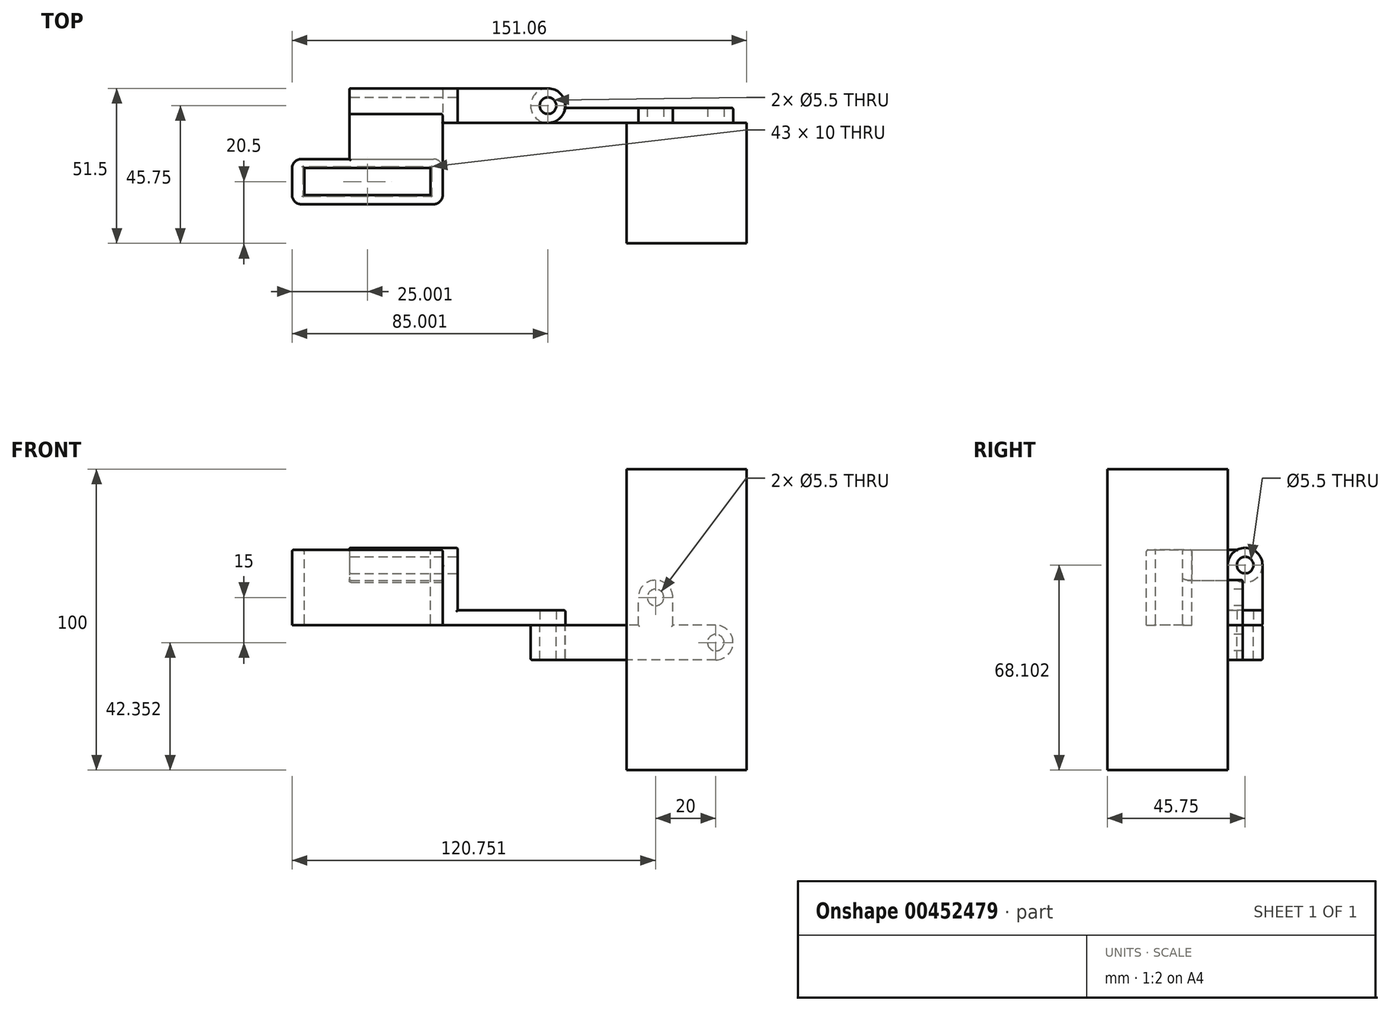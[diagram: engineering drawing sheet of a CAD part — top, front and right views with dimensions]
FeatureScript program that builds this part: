
annotation { "Feature Type Name" : "Feature", "Feature Type Description" : "" }
export const myFeature = defineFeature(function(context is Context, id is Id, definition is map)
    precondition{}
    {
        {
            var Q0;
            Q0=qCreatedBy(makeId("Top.planeOp"),FACE);
            var sketch = newSketch(context, id + "F0", { "sketchPlane" : qUnion([Q0])});
            skLineSegment(sketch, "E0.bottom", {"start": v(-20, 20) * mm, "end": v(20, 20) * mm});
            skLineSegment(sketch, "E0.top", {"start": v(-20, -20) * mm, "end": v(20, -20) * mm});
            skLineSegment(sketch, "E0.left", {"start": v(-20, 20) * mm, "end": v(-20, -20) * mm});
            skLineSegment(sketch, "E0.right", {"start": v(20, 20) * mm, "end": v(20, -20) * mm});
            skPoint(sketch, "E0.middle", {"position": v(0, 0) * mm});
            skSolve(sketch);
        }
        {
            var Q0;
            Q0=makeQuery(id+"F0.imprint","IMPRINT",FACE,{"disambiguationData":[TD([[makeQuery(id+"F0.imprint","IMPRINT",EDGE,{"derivedFrom":sQuery(id+"F0.wireOp",EDGE,"E0.bottom")}),-1.0]])]});
            extrude(context, id + "F1", {"entities" : qUnion([Q0]), "depth" : 100 * mm});
        }
        {
            var Q0;
            Q0=makeQuery(id+"F1.opExtrude","SWEPT_FACE",FACE,{"disambiguationData":[OSD([sQuery(id+"F0.wireOp",EDGE,"E0.bottom")])]});
            var sketch = newSketch(context, id + "F2", { "sketchPlane" : qUnion([Q0])});
            skPoint(sketch, "E1", {"position": v(-9.7, 42.35) * mm});
            skPoint(sketch, "E2", {"position": v(10.3, 57.35) * mm});
            skCircle(sketch, "E3", {"center": v(-9.7, 42.35) * mm, "radius": 5.75 * mm});
            skCircle(sketch, "E4", {"center": v(10.3, 57.35) * mm, "radius": 5.75 * mm});
            skLineSegment(sketch, "E5", {"start": v(-9.7, 48.1) * mm, "end": v(4.56, 48.1) * mm});
            skLineSegment(sketch, "E6", {"start": v(4.56, 48.1) * mm, "end": v(4.56, 57.35) * mm});
            skLineSegment(sketch, "E7", {"start": v(-9.7, 36.6) * mm, "end": v(16.06, 36.6) * mm});
            skLineSegment(sketch, "E8", {"start": v(16.06, 36.6) * mm, "end": v(16.06, 57.35) * mm});
            skLineSegment(sketch, "E9", {"start": v(16.06, 48.1) * mm, "end": v(46.06, 48.1) * mm});
            skLineSegment(sketch, "E10", {"start": v(46.06, 48.1) * mm, "end": v(46.06, 36.6) * mm});
            skLineSegment(sketch, "E11", {"start": v(46.06, 36.6) * mm, "end": v(16.06, 36.6) * mm});
            skSolve(sketch);
        }
        {
            var Q0;
            {var subQ0=sQuery(id+"F2.wireOp",EDGE,"E3");var subQ1=makeQuery(id+"F2.imprint","INTERSECT",VERTEX,{"derivedFrom":[subQ0,sQuery(id+"F2.wireOp",EDGE,"E5")]});Q0=makeQuery(id+"F2.imprint","IMPRINT",FACE,{"disambiguationData":[TD([[makeQuery(id+"F2.imprint","IMPRINT",EDGE,{"disambiguationData":[TD([[subQ1,-1.0]])],"derivedFrom":subQ0}),1.0]])]});}
            var Q1;
            {var subQ0=sQuery(id+"F2.wireOp",EDGE,"E4");var subQ1=makeQuery(id+"F2.imprint","INTERSECT",VERTEX,{"derivedFrom":[subQ0,sQuery(id+"F2.wireOp",EDGE,"E6")]});Q1=makeQuery(id+"F2.imprint","IMPRINT",FACE,{"disambiguationData":[TD([[makeQuery(id+"F2.imprint","IMPRINT",EDGE,{"disambiguationData":[TD([[subQ1,1.0]])],"derivedFrom":subQ0}),1.0]])]});}
            var Q2;
            {var subQ1=sQuery(id+"F2.wireOp",EDGE,"E5");Q2=makeQuery(id+"F2.imprint","IMPRINT",FACE,{"disambiguationData":[TD([[makeQuery(id+"F2.imprint","IMPRINT",EDGE,{"derivedFrom":subQ1}),-1.0]])]});}
            var Q3;
            {var subQ0=sQuery(id+"F2.wireOp",EDGE,"E10");Q3=makeQuery(id+"F2.imprint","IMPRINT",FACE,{"disambiguationData":[TD([[makeQuery(id+"F2.imprint","IMPRINT",EDGE,{"derivedFrom":subQ0}),-1.0]])]});}
            var Q4;
            {var subQ1=sQuery(id+"F2.wireOp",EDGE,"E8");var subQ3=sQuery(id+"F2.wireOp",EDGE,"E9");var subQ4=makeQuery(id+"F2.imprint","INTERSECT",VERTEX,{"derivedFrom":[subQ1,subQ3]});Q4=makeQuery(id+"F2.imprint","IMPRINT",FACE,{"disambiguationData":[TD([[makeQuery(id+"F2.imprint","IMPRINT",EDGE,{"disambiguationData":[TD([[subQ4,1.0]])],"derivedFrom":subQ1}),-1.0]])]});}
            extrude(context, id + "F3", {"entities" : qUnion([Q0, Q1, Q2, Q3, Q4]), "depth" : 5 * mm});
        }
        {
            var Q0;
            Q0=sQuery(id+"F2.wireOp",VERTEX,"E2");
            var Q1;
            Q1=sQuery(id+"F2.wireOp",VERTEX,"E1");
            var Q2;
            Q2=makeQuery(id+"F3.opExtrude","SWEPT_BODY",BODY,{"disambiguationData":[OSD([sQuery(id+"F2.wireOp",EDGE,"E3"),sQuery(id+"F2.wireOp",EDGE,"E4"),sQuery(id+"F2.wireOp",EDGE,"E5"),sQuery(id+"F2.wireOp",EDGE,"E6"),sQuery(id+"F2.wireOp",EDGE,"E7"),sQuery(id+"F2.wireOp",EDGE,"E8"),sQuery(id+"F2.wireOp",EDGE,"E9"),sQuery(id+"F2.wireOp",EDGE,"E10"),sQuery(id+"F2.wireOp",EDGE,"E11")])]});
            hole(context, id + "F4", {"style" : HoleStyle.SIMPLE, "endStyle" : HoleEndStyle.THROUGH, "oppositeDirection" : true, "standardTappedOrClearance" : lookupTablePath({ "standard" : "ISO", "fit" : "Normal", "size" : "M5", "type" : "Clearance" }), "standardBlindInLast" : lookupTablePath({ "fit" : "Standard", "standard" : "ISO", "size" : "M5", "type" : "Clearance" }), "holeDiameter" : 5.5 * mm, "isTappedThrough" : true, "tappedDepth" : 13.2 * mm, "tapClearance" : 3, "startFromSketch" : true, "locations" : qUnion([Q0, Q1]), "scope" : qUnion([Q2])});
        }
        {
            var Q0;
            Q0=makeQuery(id+"F3.opExtrude","SWEPT_FACE",FACE,{"disambiguationData":[OSD([sQuery(id+"F2.wireOp",EDGE,"E9")])]});
            var sketch = newSketch(context, id + "F5", { "sketchPlane" : qUnion([Q0])});
            skPoint(sketch, "E12", {"position": v(-46.06, 25.75) * mm});
            skCircle(sketch, "E13", {"center": v(-46.06, 25.75) * mm, "radius": 5.75 * mm});
            skSolve(sketch);
        }
        {
            var Q0;
            {var subQ1=sQuery(id+"F2.wireOp",EDGE,"E9");var subQ2=makeQuery(id+"F3.opExtrude","SWEPT_EDGE",EDGE,{"disambiguationData":[OSD([subQ1,sQuery(id+"F2.wireOp",EDGE,"E10")])]});Q0=makeQuery(id+"F5.imprint","IMPRINT",FACE,{"disambiguationData":[TD([[makeQuery(id+"F5.imprint","IMPRINT",EDGE,{"derivedFrom":subQ2}),-1.0]])]});}
            var Q1;
            Q1=makeQuery(id+"F3.opExtrude","SWEPT_FACE",FACE,{"disambiguationData":[OSD([sQuery(id+"F2.wireOp",EDGE,"E7"),sQuery(id+"F2.wireOp",EDGE,"E11")])]});
            extrude(context, id + "F6", {"entities" : qUnion([Q0]), "operationType" : NewBodyOperationType.ADD, "endBound" : BoundingType.UP_TO_SURFACE, "oppositeDirection" : true, "endBoundEntityFace" : qUnion([Q1]), "depth" : 25 * mm});
        }
        {
            var Q0;
            Q0=sQuery(id+"F5.wireOp",VERTEX,"E12");
            var Q1;
            Q1=makeQuery(id+"F3.opExtrude","SWEPT_BODY",BODY,{"disambiguationData":[OSD([sQuery(id+"F2.wireOp",EDGE,"E3"),sQuery(id+"F2.wireOp",EDGE,"E4"),sQuery(id+"F2.wireOp",EDGE,"E5"),sQuery(id+"F2.wireOp",EDGE,"E6"),sQuery(id+"F2.wireOp",EDGE,"E7"),sQuery(id+"F2.wireOp",EDGE,"E8"),sQuery(id+"F2.wireOp",EDGE,"E9"),sQuery(id+"F2.wireOp",EDGE,"E10"),sQuery(id+"F2.wireOp",EDGE,"E11")])]});
            hole(context, id + "F7", {"style" : HoleStyle.SIMPLE, "endStyle" : HoleEndStyle.THROUGH, "standardTappedOrClearance" : lookupTablePath({ "standard" : "ISO", "fit" : "Normal", "size" : "M5", "type" : "Clearance" }), "standardBlindInLast" : lookupTablePath({ "fit" : "Standard", "standard" : "ISO", "size" : "M5", "type" : "Clearance" }), "holeDiameter" : 5.5 * mm, "isTappedThrough" : true, "tappedDepth" : 13.2 * mm, "tapClearance" : 3, "startFromSketch" : true, "locations" : qUnion([Q0]), "scope" : qUnion([Q1])});
        }
        {
            var Q0;
            {var subQ1=sQuery(id+"F2.wireOp",EDGE,"E9");var subQ2=makeQuery(id+"F3.opExtrude","CAP_EDGE",EDGE,{"disambiguationData":[OSD([subQ1])],"isStart":true});Q0=makeQuery(id+"F5.imprint","IMPRINT",FACE,{"disambiguationData":[TD([[makeQuery(id+"F5.imprint","IMPRINT",EDGE,{"derivedFrom":subQ2}),-1.0]])]});}
            var sketch = newSketch(context, id + "F8", { "sketchPlane" : qUnion([Q0])});
            skPoint(sketch, "E14", {"position": v(-46.06, 25.75) * mm});
            skCircle(sketch, "E15", {"center": v(-46.06, 25.75) * mm, "radius": 5.75 * mm});
            skLineSegment(sketch, "E16", {"start": v(-46.06, 31.5) * mm, "end": v(-76.06, 31.5) * mm});
            skLineSegment(sketch, "E17", {"start": v(-76.06, 31.5) * mm, "end": v(-76.06, 20) * mm});
            skLineSegment(sketch, "E18", {"start": v(-76.06, 20) * mm, "end": v(-46.06, 20) * mm});
            skSolve(sketch);
        }
        {
            var Q0;
            {var subQ2=sQuery(id+"F8.wireOp",EDGE,"E16");Q0=makeQuery(id+"F8.imprint","IMPRINT",FACE,{"disambiguationData":[TD([[makeQuery(id+"F8.imprint","IMPRINT",EDGE,{"derivedFrom":subQ2}),1.0]])]});}
            var Q1;
            {var subQ0=sQuery(id+"F8.wireOp",EDGE,"E15");var subQ3=makeQuery(id+"F8.imprint","INTERSECT",VERTEX,{"derivedFrom":[subQ0,sQuery(id+"F8.wireOp",EDGE,"E16")]});Q1=makeQuery(id+"F8.imprint","IMPRINT",FACE,{"disambiguationData":[TD([[makeQuery(id+"F8.imprint","IMPRINT",EDGE,{"disambiguationData":[TD([[subQ3,-1.0]])],"derivedFrom":subQ0}),1.0]])]});}
            extrude(context, id + "F9", {"entities" : qUnion([Q0, Q1]), "depth" : 5 * mm});
        }
        {
            var Q0;
            Q0=sQuery(id+"F5.wireOp",VERTEX,"E12");
            var Q1;
            Q1=makeQuery(id+"F9.opExtrude","SWEPT_BODY",BODY,{"disambiguationData":[OSD([sQuery(id+"F8.wireOp",EDGE,"E15"),sQuery(id+"F8.wireOp",EDGE,"E16"),sQuery(id+"F8.wireOp",EDGE,"E17"),sQuery(id+"F8.wireOp",EDGE,"E18")])]});
            hole(context, id + "F10", {"style" : HoleStyle.SIMPLE, "endStyle" : HoleEndStyle.THROUGH, "oppositeDirection" : true, "standardTappedOrClearance" : lookupTablePath({ "standard" : "ISO", "fit" : "Normal", "size" : "M5", "type" : "Clearance" }), "standardBlindInLast" : lookupTablePath({ "fit" : "Standard", "standard" : "ISO", "size" : "M5", "type" : "Clearance" }), "holeDiameter" : 5.5 * mm, "isTappedThrough" : true, "tappedDepth" : 13.2 * mm, "tapClearance" : 3, "startFromSketch" : true, "locations" : qUnion([Q0]), "scope" : qUnion([Q1])});
        }
        {
            var Q0;
            Q0=makeQuery(id+"F9.opExtrude","SWEPT_FACE",FACE,{"disambiguationData":[OSD([sQuery(id+"F8.wireOp",EDGE,"E17")])]});
            var sketch = newSketch(context, id + "F11", { "sketchPlane" : qUnion([Q0])});
            skLineSegment(sketch, "E19.bottom", {"start": v(-31.5, 48.1) * mm, "end": v(-20, 48.1) * mm});
            skLineSegment(sketch, "E19.top", {"start": v(-31.5, 68.1) * mm, "end": v(-20, 68.1) * mm});
            skLineSegment(sketch, "E19.left", {"start": v(-31.5, 48.1) * mm, "end": v(-31.5, 68.1) * mm});
            skLineSegment(sketch, "E19.right", {"start": v(-20, 48.1) * mm, "end": v(-20, 68.1) * mm});
            skCircle(sketch, "E20", {"center": v(-25.75, 68.1) * mm, "radius": 5.75 * mm});
            skSolve(sketch);
        }
        {
            var Q0;
            {var subQ0=sQuery(id+"F11.wireOp",EDGE,"E19.top");Q0=makeQuery(id+"F11.imprint","IMPRINT",FACE,{"disambiguationData":[TD([[makeQuery(id+"F11.imprint","IMPRINT",EDGE,{"derivedFrom":subQ0}),-1.0]])]});}
            var Q1;
            {var subQ0=sQuery(id+"F11.wireOp",EDGE,"E19.top");Q1=makeQuery(id+"F11.imprint","IMPRINT",FACE,{"disambiguationData":[TD([[makeQuery(id+"F11.imprint","IMPRINT",EDGE,{"derivedFrom":subQ0}),1.0]])]});}
            var Q2;
            {var subQ1=makeQuery(id+"F9.opExtrude","CAP_EDGE",EDGE,{"disambiguationData":[OSD([sQuery(id+"F8.wireOp",EDGE,"E17")])],"isStart":false});Q2=makeQuery(id+"F11.imprint","IMPRINT",FACE,{"disambiguationData":[TD([[makeQuery(id+"F11.imprint","IMPRINT",EDGE,{"derivedFrom":subQ1}),1.0]])]});}
            var Q3;
            {var subQ0=sQuery(id+"F11.wireOp",EDGE,"E19.bottom");Q3=makeQuery(id+"F11.imprint","IMPRINT",FACE,{"disambiguationData":[TD([[makeQuery(id+"F11.imprint","IMPRINT",EDGE,{"derivedFrom":subQ0}),1.0]])]});}
            extrude(context, id + "F12", {"entities" : qUnion([Q0, Q1, Q2, Q3]), "operationType" : NewBodyOperationType.ADD, "depth" : 5 * mm});
        }
        {
            var Q0;
            Q0=sQuery(id+"F11.wireOp",VERTEX,"E20.center");
            var Q1;
            Q1=makeQuery(id+"F9.opExtrude","SWEPT_BODY",BODY,{"disambiguationData":[OSD([sQuery(id+"F8.wireOp",EDGE,"E15"),sQuery(id+"F8.wireOp",EDGE,"E16"),sQuery(id+"F8.wireOp",EDGE,"E17"),sQuery(id+"F8.wireOp",EDGE,"E18")])]});
            hole(context, id + "F13", {"style" : HoleStyle.SIMPLE, "endStyle" : HoleEndStyle.THROUGH, "oppositeDirection" : true, "standardTappedOrClearance" : lookupTablePath({ "standard" : "ISO", "fit" : "Normal", "size" : "M5", "type" : "Clearance" }), "standardBlindInLast" : lookupTablePath({ "fit" : "Standard", "standard" : "ISO", "size" : "M5", "type" : "Clearance" }), "holeDiameter" : 5.5 * mm, "isTappedThrough" : true, "tappedDepth" : 13.2 * mm, "tapClearance" : 3, "startFromSketch" : true, "locations" : qUnion([Q0]), "scope" : qUnion([Q1])});
        }
        {
            var Q0;
            Q0=makeQuery(id+"F12.opExtrude","CAP_FACE",FACE,{"disambiguationData":[OSD([sQuery(id+"F11.wireOp",EDGE,"E19.bottom"),sQuery(id+"F11.wireOp",EDGE,"E19.left"),sQuery(id+"F11.wireOp",EDGE,"E19.right"),sQuery(id+"F11.wireOp",EDGE,"E20")])],"isStart":false});
            var sketch = newSketch(context, id + "F14", { "sketchPlane" : qUnion([Q0])});
            skCircle(sketch, "E21", {"center": v(-25.75, 68.1) * mm, "radius": 5.75 * mm});
            skSolve(sketch);
        }
        {
            var Q0;
            {var subQ0=sQuery(id+"F14.wireOp",EDGE,"E21");var subQ1=sQuery(id+"F11.wireOp",EDGE,"E19.left");var subQ2=makeQuery(id+"F14.imprint","INTERSECT",VERTEX,{"derivedFrom":[makeQuery(id+"F12.opExtrude","CAP_EDGE",EDGE,{"disambiguationData":[OSD([subQ1])],"isStart":false}),subQ0]});Q0=makeQuery(id+"F14.imprint","IMPRINT",FACE,{"disambiguationData":[TD([[makeQuery(id+"F14.imprint","IMPRINT",EDGE,{"disambiguationData":[TD([[subQ2,1.0]])],"derivedFrom":subQ0}),1.0]])]});}
            extrude(context, id + "F15", {"entities" : qUnion([Q0]), "depth" : 31 * mm});
        }
        {
            var Q0;
            Q0=makeQuery(id+"F15.opExtrude","CAP_FACE",FACE,{"disambiguationData":[OSD([sQuery(id+"F11.wireOp",EDGE,"E19.bottom"),sQuery(id+"F11.wireOp",EDGE,"E19.left"),sQuery(id+"F11.wireOp",EDGE,"E19.right"),sQuery(id+"F11.wireOp",EDGE,"E20"),sQuery(id+"F13.hole-0.sketch.wireOp",EDGE,"core_line_2"),sQuery(id+"F14.wireOp",EDGE,"E21")])],"isStart":true});
            var sketch = newSketch(context, id + "F16", { "sketchPlane" : qUnion([Q0])});
            skLineSegment(sketch, "E22.bottom", {"start": v(8, 73.15) * mm, "end": v(23, 73.15) * mm});
            skLineSegment(sketch, "E22.top", {"start": v(8, 63.05) * mm, "end": v(23, 63.05) * mm});
            skLineSegment(sketch, "E22.left", {"start": v(8, 73.15) * mm, "end": v(8, 63.05) * mm});
            skLineSegment(sketch, "E22.right", {"start": v(23, 73.15) * mm, "end": v(23, 63.05) * mm});
            skSolve(sketch);
        }
        {
            var Q0;
            {var subQ0=sQuery(id+"F16.wireOp",EDGE,"E22.bottom");Q0=makeQuery(id+"F16.imprint","IMPRINT",FACE,{"disambiguationData":[TD([[makeQuery(id+"F16.imprint","IMPRINT",EDGE,{"derivedFrom":subQ0}),-1.0]])]});}
            extrude(context, id + "F17", {"entities" : qUnion([Q0]), "operationType" : NewBodyOperationType.ADD, "oppositeDirection" : true, "depth" : 31 * mm});
        }
        {
            var Q0;
            Q0=makeQuery(id+"F17.opExtrude","SWEPT_FACE",FACE,{"disambiguationData":[OSD([sQuery(id+"F16.wireOp",EDGE,"E22.bottom")])]});
            var sketch = newSketch(context, id + "F18", { "sketchPlane" : qUnion([Q0])});
            skLineSegment(sketch, "E23.bottom", {"start": v(-81.06, 8) * mm, "end": v(-131.06, 8) * mm});
            skLineSegment(sketch, "E23.top", {"start": v(-81.06, -7) * mm, "end": v(-131.06, -7) * mm});
            skLineSegment(sketch, "E23.left", {"start": v(-81.06, 8) * mm, "end": v(-81.06, -7) * mm});
            skLineSegment(sketch, "E23.right", {"start": v(-131.06, 8) * mm, "end": v(-131.06, -7) * mm});
            skLineSegment(sketch, "E24.bottom", {"start": v(-127.06, 5) * mm, "end": v(-85.06, 5) * mm});
            skLineSegment(sketch, "E24.top", {"start": v(-127.06, -4) * mm, "end": v(-85.06, -4) * mm});
            skLineSegment(sketch, "E24.left", {"start": v(-127.06, 5) * mm, "end": v(-127.06, -4) * mm});
            skLineSegment(sketch, "E24.right", {"start": v(-85.06, 5) * mm, "end": v(-85.06, -4) * mm});
            skPoint(sketch, "E25", {"position": v(-106.06, 5) * mm});
            skPoint(sketch, "E26", {"position": v(-85.06, 0.5) * mm});
            skPoint(sketch, "E27", {"position": v(-81.06, 0.5) * mm});
            skPoint(sketch, "E28", {"position": v(-106.06, 8) * mm});
            skSolve(sketch);
        }
        {
            var Q0;
            Q0=makeQuery(id+"F18.imprint","IMPRINT",FACE,{"disambiguationData":[TD([[makeQuery(id+"F18.imprint","IMPRINT",EDGE,{"derivedFrom":sQuery(id+"F18.wireOp",EDGE,"E23.top")}),-1.0]])]});
            extrude(context, id + "F19", {"entities" : qUnion([Q0]), "operationType" : NewBodyOperationType.ADD, "oppositeDirection" : true, "depth" : 25 * mm});
        }
        {
            var Q0;
            Q0=makeQuery(id+"F19.opExtrude","SWEPT_EDGE",EDGE,{"disambiguationData":[OSD([sQuery(id+"F18.wireOp",EDGE,"E23.bottom"),sQuery(id+"F18.wireOp",EDGE,"E23.right")])]});
            var Q1;
            Q1=makeQuery(id+"F19.opExtrude","SWEPT_EDGE",EDGE,{"disambiguationData":[OSD([sQuery(id+"F18.wireOp",EDGE,"E23.top"),sQuery(id+"F18.wireOp",EDGE,"E23.right")])]});
            var Q2;
            Q2=makeQuery(id+"F19.opExtrude","SWEPT_EDGE",EDGE,{"disambiguationData":[OSD([sQuery(id+"F18.wireOp",EDGE,"E23.top"),sQuery(id+"F18.wireOp",EDGE,"E23.left")])]});
            var Q3;
            Q3=makeQuery(id+"F19.opExtrude","SWEPT_EDGE",EDGE,{"disambiguationData":[OSD([sQuery(id+"F16.wireOp",EDGE,"E22.bottom"),sQuery(id+"F18.wireOp",EDGE,"E23.bottom"),sQuery(id+"F18.wireOp",EDGE,"E23.left")])]});
            fillet(context, id + "F20", {"entities" : qUnion([Q0, Q1, Q2, Q3]), "radius" : 3 * mm, "tangentPropagation" : true, "allowEdgeOverflow" : false});
        }
        {
            var Q0;
            Q0=makeQuery(id+"F17.opExtrude","CAP_EDGE",EDGE,{"disambiguationData":[OSD([sQuery(id+"F16.wireOp",EDGE,"E22.top")])],"isStart":true});
            var Q1;
            Q1=makeQuery(id+"F19.boolean.opBoolean","MERGE",EDGE,{"derivedFrom":[makeQuery(id+"F17.opExtrude","CAP_EDGE",EDGE,{"disambiguationData":[OSD([sQuery(id+"F16.wireOp",EDGE,"E22.bottom")])],"isStart":true}),makeQuery(id+"F19.opExtrude","CAP_EDGE",EDGE,{"disambiguationData":[OSD([sQuery(id+"F18.wireOp",EDGE,"E23.left")])],"isStart":true})]});
            var Q2;
            Q2=makeQuery(id+"F15.opExtrude","CAP_EDGE",EDGE,{"disambiguationData":[OSD([sQuery(id+"F14.wireOp",EDGE,"E21")])],"isStart":true});
            var Q3;
            Q3=makeQuery(id+"F15.opExtrude","CAP_EDGE",EDGE,{"disambiguationData":[OSD([sQuery(id+"F11.wireOp",EDGE,"E19.bottom"),sQuery(id+"F11.wireOp",EDGE,"E19.left"),sQuery(id+"F11.wireOp",EDGE,"E19.right"),sQuery(id+"F11.wireOp",EDGE,"E20"),sQuery(id+"F13.hole-0.sketch.wireOp",EDGE,"core_line_2")])],"isStart":true});
            var Q4;
            Q4=makeQuery(id+"F19.opExtrude","CAP_EDGE",EDGE,{"disambiguationData":[OSD([sQuery(id+"F18.wireOp",EDGE,"E24.top")])],"isStart":true});
            var Q5;
            Q5=makeQuery(id+"F19.opExtrude","CAP_EDGE",EDGE,{"disambiguationData":[OSD([sQuery(id+"F18.wireOp",EDGE,"E24.right")])],"isStart":true});
            var Q6;
            Q6=makeQuery(id+"F19.opExtrude","CAP_EDGE",EDGE,{"disambiguationData":[OSD([sQuery(id+"F18.wireOp",EDGE,"E24.bottom")])],"isStart":true});
            var Q7;
            Q7=makeQuery(id+"F19.opExtrude","CAP_EDGE",EDGE,{"disambiguationData":[OSD([sQuery(id+"F18.wireOp",EDGE,"E24.left")])],"isStart":true});
            var Q8;
            Q8=makeQuery(id+"F17.opExtrude","CAP_EDGE",EDGE,{"disambiguationData":[OSD([sQuery(id+"F16.wireOp",EDGE,"E22.bottom")])],"isStart":false});
            var Q9;
            Q9=makeQuery(id+"F15.opExtrude","CAP_EDGE",EDGE,{"disambiguationData":[OSD([sQuery(id+"F14.wireOp",EDGE,"E21")])],"isStart":false});
            var Q10;
            Q10=makeQuery(id+"F17.opExtrude","CAP_EDGE",EDGE,{"disambiguationData":[OSD([sQuery(id+"F16.wireOp",EDGE,"E22.top")])],"isStart":false});
            var Q11;
            Q11=makeQuery(id+"F15.opExtrude","CAP_EDGE",EDGE,{"disambiguationData":[OSD([sQuery(id+"F11.wireOp",EDGE,"E19.bottom"),sQuery(id+"F11.wireOp",EDGE,"E19.left"),sQuery(id+"F11.wireOp",EDGE,"E19.right"),sQuery(id+"F11.wireOp",EDGE,"E20"),sQuery(id+"F13.hole-0.sketch.wireOp",EDGE,"core_line_2")])],"isStart":false});
            var Q12;
            Q12=makeQuery(id+"F17.opExtrude","CAP_EDGE",EDGE,{"disambiguationData":[OSD([sQuery(id+"F16.wireOp",EDGE,"E22.left")])],"isStart":false});
            var Q13;
            Q13=makeQuery(id+"F17.opExtrude","SWEPT_EDGE",EDGE,{"disambiguationData":[OSD([sQuery(id+"F16.wireOp",EDGE,"E22.top"),sQuery(id+"F16.wireOp",EDGE,"E22.left")])]});
            var Q14;
            Q14=makeQuery(id+"F19.opExtrude","CAP_EDGE",EDGE,{"disambiguationData":[OSD([sQuery(id+"F18.wireOp",EDGE,"E24.bottom")])],"isStart":false});
            var Q15;
            Q15=makeQuery(id+"F19.opExtrude","CAP_EDGE",EDGE,{"disambiguationData":[OSD([sQuery(id+"F18.wireOp",EDGE,"E24.left")])],"isStart":false});
            var Q16;
            Q16=makeQuery(id+"F19.opExtrude","CAP_EDGE",EDGE,{"disambiguationData":[OSD([sQuery(id+"F18.wireOp",EDGE,"E24.top")])],"isStart":false});
            var Q17;
            Q17=makeQuery(id+"F19.opExtrude","CAP_EDGE",EDGE,{"disambiguationData":[OSD([sQuery(id+"F18.wireOp",EDGE,"E24.right")])],"isStart":false});
            var Q18;
            Q18=makeQuery(id+"F13.hole-0.boolean.opBoolean","INTERSECT",EDGE,{"derivedFrom":[makeQuery(id+"F12.opExtrude","CAP_FACE",FACE,{"disambiguationData":[OSD([sQuery(id+"F11.wireOp",EDGE,"E19.bottom"),sQuery(id+"F11.wireOp",EDGE,"E19.left"),sQuery(id+"F11.wireOp",EDGE,"E19.right"),sQuery(id+"F11.wireOp",EDGE,"E20")])],"isStart":false}),makeQuery(id+"F13.hole-0.opRevolve","SWEPT_FACE",FACE,{"disambiguationData":[OSD([sQuery(id+"F13.hole-0.sketch.wireOp",EDGE,"core_line_2")])]})]});
            var Q19;
            Q19=makeQuery(id+"F13.hole-0.boolean.opBoolean","COPY",EDGE,{"derivedFrom":makeQuery(id+"F13.hole-0.opRevolve","SWEPT_EDGE",EDGE,{"disambiguationData":[OSD([sQuery(id+"F13.hole-0.sketch.wireOp",EDGE,"core_line_2"),sQuery(id+"F13.hole-0.sketch.wireOp",EDGE,"core_line_3")])]})});
            var Q20;
            Q20=makeQuery(id+"F7.hole-0.boolean.opBoolean","COPY",EDGE,{"derivedFrom":makeQuery(id+"F7.hole-0.opRevolve","SWEPT_EDGE",EDGE,{"disambiguationData":[OSD([sQuery(id+"F7.hole-0.sketch.wireOp",EDGE,"core_line_2"),sQuery(id+"F7.hole-0.sketch.wireOp",EDGE,"core_line_3")])]})});
            var Q21;
            Q21=makeQuery(id+"F10.hole-0.boolean.opBoolean","INTERSECT",EDGE,{"derivedFrom":[makeQuery(id+"F9.opExtrude","CAP_FACE",FACE,{"disambiguationData":[OSD([sQuery(id+"F8.wireOp",EDGE,"E15"),sQuery(id+"F8.wireOp",EDGE,"E16"),sQuery(id+"F8.wireOp",EDGE,"E17"),sQuery(id+"F8.wireOp",EDGE,"E18")])],"isStart":false}),makeQuery(id+"F10.hole-0.opRevolve","SWEPT_FACE",FACE,{"disambiguationData":[OSD([sQuery(id+"F10.hole-0.sketch.wireOp",EDGE,"core_line_2")])]})]});
            var Q22;
            Q22=makeQuery(id+"F9.opExtrude","CAP_EDGE",EDGE,{"disambiguationData":[OSD([sQuery(id+"F8.wireOp",EDGE,"E16")])],"isStart":false});
            var Q23;
            Q23=makeQuery(id+"F12.opExtrude","CAP_EDGE",EDGE,{"disambiguationData":[OSD([sQuery(id+"F11.wireOp",EDGE,"E19.left")])],"isStart":true});
            var Q24;
            Q24=makeQuery(id+"F12.boolean.opBoolean","MERGE",EDGE,{"derivedFrom":[makeQuery(id+"F9.opExtrude","CAP_EDGE",EDGE,{"disambiguationData":[OSD([sQuery(id+"F8.wireOp",EDGE,"E18")])],"isStart":true}),makeQuery(id+"F12.opExtrude","SWEPT_EDGE",EDGE,{"disambiguationData":[OSD([sQuery(id+"F11.wireOp",EDGE,"E19.bottom"),sQuery(id+"F11.wireOp",EDGE,"E19.right")])]})]});
            var Q25;
            Q25=makeQuery(id+"F12.opExtrude","CAP_EDGE",EDGE,{"disambiguationData":[OSD([sQuery(id+"F11.wireOp",EDGE,"E19.bottom")])],"isStart":false});
            var Q26;
            Q26=makeQuery(id+"F12.opExtrude","CAP_EDGE",EDGE,{"disambiguationData":[OSD([sQuery(id+"F11.wireOp",EDGE,"E19.left")])],"isStart":false});
            var Q27;
            Q27=makeQuery(id+"F7.hole-0.boolean.opBoolean","INTERSECT",EDGE,{"derivedFrom":[makeQuery(id+"F6.boolean.opBoolean","MERGE",FACE,{"derivedFrom":[makeQuery(id+"F3.opExtrude","SWEPT_FACE",FACE,{"disambiguationData":[OSD([sQuery(id+"F2.wireOp",EDGE,"E7"),sQuery(id+"F2.wireOp",EDGE,"E11")])]}),makeQuery(id+"F6.opExtrude","CAP_FACE",FACE,{"disambiguationData":[OSD([sQuery(id+"F2.wireOp",EDGE,"E9"),sQuery(id+"F2.wireOp",EDGE,"E10"),sQuery(id+"F5.wireOp",EDGE,"E13")])],"isStart":false})]}),makeQuery(id+"F7.hole-0.opRevolve","SWEPT_FACE",FACE,{"disambiguationData":[OSD([sQuery(id+"F7.hole-0.sketch.wireOp",EDGE,"core_line_2")])]})]});
            var Q28;
            Q28=makeQuery(id+"F6.opExtrude","CAP_EDGE",EDGE,{"disambiguationData":[OSD([sQuery(id+"F5.wireOp",EDGE,"E13")])],"isStart":false});
            var Q29;
            Q29=makeQuery(id+"F3.opExtrude","CAP_EDGE",EDGE,{"disambiguationData":[OSD([sQuery(id+"F2.wireOp",EDGE,"E7"),sQuery(id+"F2.wireOp",EDGE,"E11")])],"isStart":false});
            var Q30;
            Q30=makeQuery(id+"F3.opExtrude","CAP_EDGE",EDGE,{"disambiguationData":[OSD([sQuery(id+"F2.wireOp",EDGE,"E9")])],"isStart":false});
            var Q31;
            Q31=makeQuery(id+"F6.opExtrude","CAP_EDGE",EDGE,{"disambiguationData":[OSD([sQuery(id+"F5.wireOp",EDGE,"E13")])],"isStart":true});
            var Q32;
            Q32=makeQuery(id+"F3.opExtrude","CAP_EDGE",EDGE,{"disambiguationData":[OSD([sQuery(id+"F2.wireOp",EDGE,"E8")])],"isStart":false});
            var Q33;
            Q33=makeQuery(id+"F3.opExtrude","CAP_EDGE",EDGE,{"disambiguationData":[OSD([sQuery(id+"F2.wireOp",EDGE,"E8")])],"isStart":true});
            var Q34;
            Q34=makeQuery(id+"F4.hole-0.boolean.opBoolean","COPY",EDGE,{"derivedFrom":makeQuery(id+"F4.hole-0.opRevolve","SWEPT_EDGE",EDGE,{"disambiguationData":[OSD([sQuery(id+"F4.hole-0.sketch.wireOp",EDGE,"core_line_2"),sQuery(id+"F4.hole-0.sketch.wireOp",EDGE,"core_line_3")])]})});
            var Q35;
            Q35=makeQuery(id+"F4.hole-0.boolean.opBoolean","INTERSECT",EDGE,{"derivedFrom":[makeQuery(id+"F3.opExtrude","CAP_FACE",FACE,{"disambiguationData":[OSD([sQuery(id+"F2.wireOp",EDGE,"E3"),sQuery(id+"F2.wireOp",EDGE,"E4"),sQuery(id+"F2.wireOp",EDGE,"E5"),sQuery(id+"F2.wireOp",EDGE,"E6"),sQuery(id+"F2.wireOp",EDGE,"E7"),sQuery(id+"F2.wireOp",EDGE,"E8"),sQuery(id+"F2.wireOp",EDGE,"E9"),sQuery(id+"F2.wireOp",EDGE,"E10"),sQuery(id+"F2.wireOp",EDGE,"E11")])],"isStart":false}),makeQuery(id+"F4.hole-0.opRevolve","SWEPT_FACE",FACE,{"disambiguationData":[OSD([sQuery(id+"F4.hole-0.sketch.wireOp",EDGE,"core_line_2")])]})]});
            var Q36;
            Q36=makeQuery(id+"F4.hole-1.boolean.opBoolean","COPY",EDGE,{"derivedFrom":makeQuery(id+"F4.hole-1.opRevolve","SWEPT_EDGE",EDGE,{"disambiguationData":[OSD([sQuery(id+"F4.hole-1.sketch.wireOp",EDGE,"core_line_2"),sQuery(id+"F4.hole-1.sketch.wireOp",EDGE,"core_line_3")])]})});
            var Q37;
            Q37=makeQuery(id+"F4.hole-1.boolean.opBoolean","INTERSECT",EDGE,{"derivedFrom":[makeQuery(id+"F3.opExtrude","CAP_FACE",FACE,{"disambiguationData":[OSD([sQuery(id+"F2.wireOp",EDGE,"E3"),sQuery(id+"F2.wireOp",EDGE,"E4"),sQuery(id+"F2.wireOp",EDGE,"E5"),sQuery(id+"F2.wireOp",EDGE,"E6"),sQuery(id+"F2.wireOp",EDGE,"E7"),sQuery(id+"F2.wireOp",EDGE,"E8"),sQuery(id+"F2.wireOp",EDGE,"E9"),sQuery(id+"F2.wireOp",EDGE,"E10"),sQuery(id+"F2.wireOp",EDGE,"E11")])],"isStart":false}),makeQuery(id+"F4.hole-1.opRevolve","SWEPT_FACE",FACE,{"disambiguationData":[OSD([sQuery(id+"F4.hole-1.sketch.wireOp",EDGE,"core_line_2")])]})]});
            fillet(context, id + "F21", {"entities" : qUnion([Q0, Q1, Q2, Q3, Q4, Q5, Q6, Q7, Q8, Q9, Q10, Q11, Q12, Q13, Q14, Q15, Q16, Q17, Q18, Q19, Q20, Q21, Q22, Q23, Q24, Q25, Q26, Q27, Q28, Q29, Q30, Q31, Q32, Q33, Q34, Q35, Q36, Q37]), "radius" : 0.5 * mm, "tangentPropagation" : true, "allowEdgeOverflow" : false});
        }
    });
